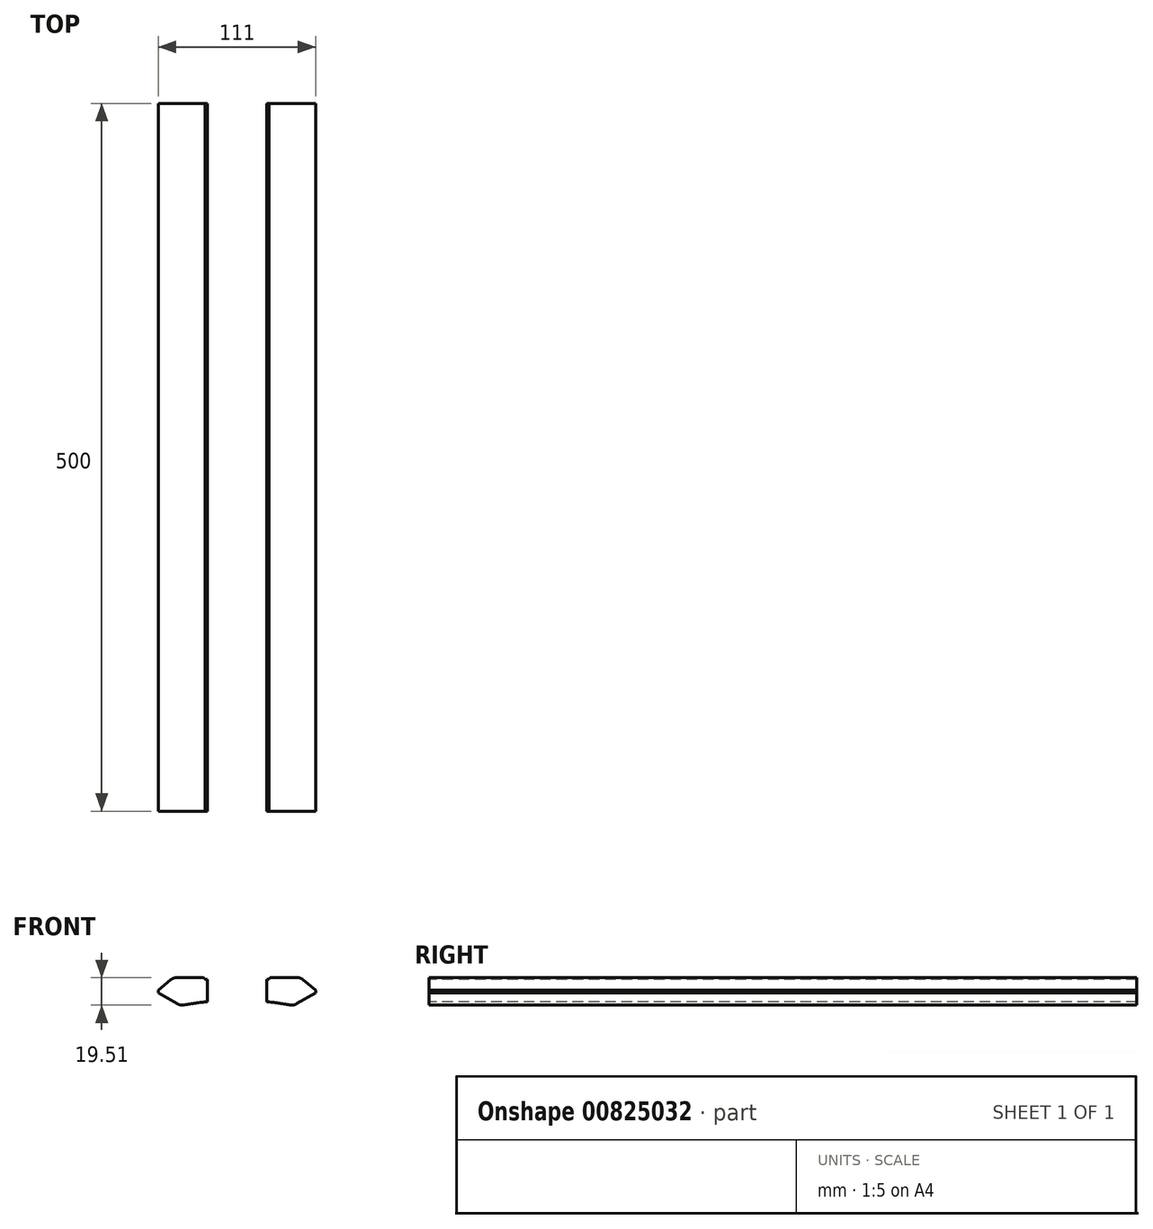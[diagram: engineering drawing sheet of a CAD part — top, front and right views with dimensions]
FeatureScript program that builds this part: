
annotation { "Feature Type Name" : "Feature", "Feature Type Description" : "" }
export const myFeature = defineFeature(function(context is Context, id is Id, definition is map)
    precondition{}
    {
        {
            var Q0;
            Q0=qCreatedBy(makeId("Front.planeOp"),FACE);
            var sketch = newSketch(context, id + "F0", { "sketchPlane" : qUnion([Q0])});
            skLineSegment(sketch, "E0", {"start": v(0, 30) * mm, "end": v(0, -27.09) * mm, "construction": true});
            skLineSegment(sketch, "E1", {"start": v(-40.18, -7.33) * mm, "end": v(-57.5, 2.67) * mm});
            skLineSegment(sketch, "E2", {"start": v(-57.5, 2.67) * mm, "end": v(-57.5, 6.67) * mm});
            skLineSegment(sketch, "E3", {"start": v(-57.5, 6.67) * mm, "end": v(-45.58, 16.67) * mm});
            skLineSegment(sketch, "E4", {"start": v(-45.58, 16.67) * mm, "end": v(-22.5, 16.67) * mm});
            skLineSegment(sketch, "E5", {"start": v(-22.5, 16.67) * mm, "end": v(-22.5, 15.37) * mm});
            skLineSegment(sketch, "E6", {"start": v(-22.5, 15.37) * mm, "end": v(0, 15.37) * mm});
            skLineSegment(sketch, "E7.MirrorCS", {"start": v(40.18, -7.33) * mm, "end": v(57.5, 2.67) * mm});
            skLineSegment(sketch, "E8.MirrorCS", {"start": v(57.5, 2.67) * mm, "end": v(57.5, 6.67) * mm});
            skLineSegment(sketch, "E9.MirrorCS", {"start": v(57.5, 6.67) * mm, "end": v(45.58, 16.67) * mm});
            skLineSegment(sketch, "E10.MirrorCS", {"start": v(22.5, 15.37) * mm, "end": v(0, 15.37) * mm});
            skLineSegment(sketch, "E11.MirrorCS", {"start": v(22.5, 16.67) * mm, "end": v(22.5, 15.37) * mm});
            skLineSegment(sketch, "E12.MirrorCS", {"start": v(45.58, 16.67) * mm, "end": v(22.5, 16.67) * mm});
            skArc(sketch, "E13", {"start": v(40.18, -7.33) * mm, "mid": v(0, -3.25) * mm, "end": v(-40.18, -7.33) * mm});
            skSolve(sketch);
        }
        {
            var Q0;
            Q0=makeQuery(id+"F0.imprint","IMPRINT",FACE,{"disambiguationData":[TD([[makeQuery(id+"F0.imprint","IMPRINT",EDGE,{"derivedFrom":sQuery(id+"F0.wireOp",EDGE,"E1")}),-1.0]])]});
            extrude(context, id + "F1", {"entities" : qUnion([Q0]), "endBound" : BoundingType.SYMMETRIC, "depth" : 500 * mm, "offsetDistance" : 25 * mm});
        }
        {
            var Q0;
            Q0=makeQuery(id+"F1.opExtrude","CAP_FACE",FACE,{"disambiguationData":[OSD([sQuery(id+"F0.wireOp",EDGE,"E1"),sQuery(id+"F0.wireOp",EDGE,"E2"),sQuery(id+"F0.wireOp",EDGE,"E3"),sQuery(id+"F0.wireOp",EDGE,"E4"),sQuery(id+"F0.wireOp",EDGE,"E5"),sQuery(id+"F0.wireOp",EDGE,"E6"),sQuery(id+"F0.wireOp",EDGE,"E7.MirrorCS"),sQuery(id+"F0.wireOp",EDGE,"E8.MirrorCS"),sQuery(id+"F0.wireOp",EDGE,"E9.MirrorCS"),sQuery(id+"F0.wireOp",EDGE,"E10.MirrorCS"),sQuery(id+"F0.wireOp",EDGE,"E11.MirrorCS"),sQuery(id+"F0.wireOp",EDGE,"E12.MirrorCS"),sQuery(id+"F0.wireOp",EDGE,"E13")])],"isStart":false});
            var sketch = newSketch(context, id + "F2", { "sketchPlane" : qUnion([Q0])});
            skLineSegment(sketch, "E14.bottom", {"start": v(19, 0) * mm, "end": v(-19, 0) * mm});
            skLineSegment(sketch, "E14.top", {"start": v(19, 13.37) * mm, "end": v(-19, 13.37) * mm});
            skLineSegment(sketch, "E14.left", {"start": v(19, 0) * mm, "end": v(19, 13.37) * mm});
            skLineSegment(sketch, "E14.right", {"start": v(-19, 0) * mm, "end": v(-19, 13.37) * mm});
            skPoint(sketch, "E14.middle", {"position": v(0, 6.69) * mm});
            skSolve(sketch);
        }
        {
            var Q0;
            Q0=makeQuery(id+"F2.imprint","IMPRINT",FACE,{"disambiguationData":[TD([[makeQuery(id+"F2.imprint","IMPRINT",EDGE,{"derivedFrom":sQuery(id+"F2.wireOp",EDGE,"E14.bottom")}),-1.0]])]});
            extrude(context, id + "F3", {"entities" : qUnion([Q0]), "operationType" : NewBodyOperationType.REMOVE, "oppositeDirection" : true, "depth" : 1200 * mm, "offsetDistance" : 25 * mm});
        }
        {
            var Q0;
            Q0=makeQuery(id+"F1.opExtrude","SWEPT_EDGE",EDGE,{"disambiguationData":[OSD([sQuery(id+"F0.wireOp",EDGE,"E4"),sQuery(id+"F0.wireOp",EDGE,"E5")])]});
            var Q1;
            Q1=makeQuery(id+"F1.opExtrude","SWEPT_EDGE",EDGE,{"disambiguationData":[OSD([sQuery(id+"F0.wireOp",EDGE,"E11.MirrorCS"),sQuery(id+"F0.wireOp",EDGE,"E12.MirrorCS")])]});
            fillet(context, id + "F4", {"entities" : qUnion([Q0, Q1]), "radius" : 2 * mm, "tangentPropagation" : true, "allowEdgeOverflow" : false});
        }
        {
            var Q0;
            Q0=makeQuery(id+"F1.opExtrude","SWEPT_EDGE",EDGE,{"disambiguationData":[OSD([sQuery(id+"F0.wireOp",EDGE,"E9.MirrorCS"),sQuery(id+"F0.wireOp",EDGE,"E12.MirrorCS")])]});
            var Q1;
            Q1=makeQuery(id+"F1.opExtrude","SWEPT_EDGE",EDGE,{"disambiguationData":[OSD([sQuery(id+"F0.wireOp",EDGE,"E7.MirrorCS"),sQuery(id+"F0.wireOp",EDGE,"E13")])]});
            var Q2;
            Q2=makeQuery(id+"F1.opExtrude","SWEPT_EDGE",EDGE,{"disambiguationData":[OSD([sQuery(id+"F0.wireOp",EDGE,"E3"),sQuery(id+"F0.wireOp",EDGE,"E4")])]});
            var Q3;
            Q3=makeQuery(id+"F1.opExtrude","SWEPT_EDGE",EDGE,{"disambiguationData":[OSD([sQuery(id+"F0.wireOp",EDGE,"E1"),sQuery(id+"F0.wireOp",EDGE,"E13")])]});
            fillet(context, id + "F5", {"entities" : qUnion([Q0, Q1, Q2, Q3]), "radius" : 9 * mm, "tangentPropagation" : true, "allowEdgeOverflow" : false});
        }
        {
            var Q0;
            Q0=makeQuery(id+"F1.opExtrude","SWEPT_EDGE",EDGE,{"disambiguationData":[OSD([sQuery(id+"F0.wireOp",EDGE,"E2"),sQuery(id+"F0.wireOp",EDGE,"E3")])]});
            var Q1;
            Q1=makeQuery(id+"F1.opExtrude","SWEPT_EDGE",EDGE,{"disambiguationData":[OSD([sQuery(id+"F0.wireOp",EDGE,"E1"),sQuery(id+"F0.wireOp",EDGE,"E2")])]});
            var Q2;
            Q2=makeQuery(id+"F1.opExtrude","SWEPT_EDGE",EDGE,{"disambiguationData":[OSD([sQuery(id+"F0.wireOp",EDGE,"E8.MirrorCS"),sQuery(id+"F0.wireOp",EDGE,"E9.MirrorCS")])]});
            var Q3;
            Q3=makeQuery(id+"F1.opExtrude","SWEPT_EDGE",EDGE,{"disambiguationData":[OSD([sQuery(id+"F0.wireOp",EDGE,"E7.MirrorCS"),sQuery(id+"F0.wireOp",EDGE,"E8.MirrorCS")])]});
            fillet(context, id + "F6", {"entities" : qUnion([Q0, Q1, Q2, Q3]), "radius" : 1 * mm, "tangentPropagation" : true, "allowEdgeOverflow" : false});
        }
        {
            var Q0;
            Q0=makeQuery(id+"F1.opExtrude","CAP_FACE",FACE,{"disambiguationData":[OSD([sQuery(id+"F0.wireOp",EDGE,"E1"),sQuery(id+"F0.wireOp",EDGE,"E2"),sQuery(id+"F0.wireOp",EDGE,"E3"),sQuery(id+"F0.wireOp",EDGE,"E4"),sQuery(id+"F0.wireOp",EDGE,"E5"),sQuery(id+"F0.wireOp",EDGE,"E6"),sQuery(id+"F0.wireOp",EDGE,"E7.MirrorCS"),sQuery(id+"F0.wireOp",EDGE,"E8.MirrorCS"),sQuery(id+"F0.wireOp",EDGE,"E9.MirrorCS"),sQuery(id+"F0.wireOp",EDGE,"E10.MirrorCS"),sQuery(id+"F0.wireOp",EDGE,"E11.MirrorCS"),sQuery(id+"F0.wireOp",EDGE,"E12.MirrorCS"),sQuery(id+"F0.wireOp",EDGE,"E13")])],"isStart":false});
            var sketch = newSketch(context, id + "F7", { "sketchPlane" : qUnion([Q0])});
            skLineSegment(sketch, "E15.0.0", {"start": v(-48.1, 14.57) * mm, "end": v(-57.14, 6.97) * mm});
            skArc(sketch, "E15.0.1", {"start": v(-57.14, 6.97) * mm, "mid": v(-57.4, 6.63) * mm, "end": v(-57.5, 6.2) * mm});
            skLineSegment(sketch, "E15.0.2", {"start": v(-57.5, 6.2) * mm, "end": v(-57.5, 3.25) * mm});
            skArc(sketch, "E15.0.3", {"start": v(-57.5, 3.25) * mm, "mid": v(-57.37, 2.75) * mm, "end": v(-57, 2.39) * mm});
            skLineSegment(sketch, "E15.0.4", {"start": v(-57, 2.39) * mm, "end": v(-43.1, -5.64) * mm});
            skArc(sketch, "E15.0.5", {"start": v(-43.1, -5.64) * mm, "mid": v(-40.12, -6.72) * mm, "end": v(-36.94, -6.69) * mm});
            skArc(sketch, "E15.0.6", {"start": v(-36.94, -6.69) * mm, "mid": v(0, -3.25) * mm, "end": v(36.94, -6.69) * mm});
            skArc(sketch, "E15.0.7", {"start": v(36.94, -6.69) * mm, "mid": v(40.12, -6.72) * mm, "end": v(43.1, -5.64) * mm});
            skLineSegment(sketch, "E15.0.8", {"start": v(43.1, -5.64) * mm, "end": v(57, 2.39) * mm});
            skArc(sketch, "E15.0.9", {"start": v(57, 2.39) * mm, "mid": v(57.37, 2.75) * mm, "end": v(57.5, 3.25) * mm});
            skLineSegment(sketch, "E15.0.10", {"start": v(57.5, 3.25) * mm, "end": v(57.5, 6.2) * mm});
            skArc(sketch, "E15.0.11", {"start": v(57.5, 6.2) * mm, "mid": v(57.4, 6.63) * mm, "end": v(57.14, 6.97) * mm});
            skLineSegment(sketch, "E15.0.12", {"start": v(57.14, 6.97) * mm, "end": v(48.1, 14.57) * mm});
            skArc(sketch, "E15.0.13", {"start": v(48.1, 14.57) * mm, "mid": v(45.38, 16.13) * mm, "end": v(42.3, 16.67) * mm});
            skLineSegment(sketch, "E15.0.14", {"start": v(42.3, 16.67) * mm, "end": v(24.37, 16.67) * mm});
            skArc(sketch, "E15.0.15", {"start": v(24.37, 16.67) * mm, "mid": v(23.23, 16.32) * mm, "end": v(22.5, 15.37) * mm});
            skLineSegment(sketch, "E15.0.16", {"start": v(22.5, 15.37) * mm, "end": v(-22.5, 15.37) * mm});
            skArc(sketch, "E15.0.17", {"start": v(-22.5, 15.37) * mm, "mid": v(-23.23, 16.32) * mm, "end": v(-24.37, 16.67) * mm});
            skLineSegment(sketch, "E15.0.18", {"start": v(-24.37, 16.67) * mm, "end": v(-42.3, 16.67) * mm});
            skArc(sketch, "E15.0.19", {"start": v(-42.3, 16.67) * mm, "mid": v(-45.38, 16.13) * mm, "end": v(-48.1, 14.57) * mm});
            skArc(sketch, "E16.0", {"start": v(-37.3, -4.72) * mm, "mid": v(-29.18, -3.37) * mm, "end": v(-21, -2.34) * mm});
            skArc(sketch, "E16.1", {"start": v(-42.1, -3.9) * mm, "mid": v(-39.78, -4.74) * mm, "end": v(-37.3, -4.72) * mm});
            skLineSegment(sketch, "E16.2", {"start": v(-55.5, 3.83) * mm, "end": v(-42.1, -3.9) * mm});
            skLineSegment(sketch, "E16.3", {"start": v(-24.37, 14.67) * mm, "end": v(-42.3, 14.67) * mm});
            skArc(sketch, "E16.4", {"start": v(-42.3, 14.67) * mm, "mid": v(-44.7, 14.25) * mm, "end": v(-46.8, 13.04) * mm});
            skLineSegment(sketch, "E16.5", {"start": v(-46.8, 13.04) * mm, "end": v(-55.5, 5.74) * mm});
            skLineSegment(sketch, "E16.6", {"start": v(-55.5, 5.74) * mm, "end": v(-55.5, 3.83) * mm});
            skLineSegment(sketch, "E17.0", {"start": v(-21, -2.34) * mm, "end": v(-21, 13.37) * mm});
            skLineSegment(sketch, "E18.0", {"start": v(-21, 13.37) * mm, "end": v(-22.5, 13.37) * mm});
            skArc(sketch, "E19", {"start": v(-22.5, 13.37) * mm, "mid": v(-23.23, 14.32) * mm, "end": v(-24.37, 14.67) * mm});
            skArc(sketch, "E20.MirrorCS", {"start": v(22.5, 13.37) * mm, "mid": v(23.23, 14.32) * mm, "end": v(24.37, 14.67) * mm});
            skLineSegment(sketch, "E21.MirrorCS", {"start": v(21, 13.37) * mm, "end": v(22.5, 13.37) * mm});
            skLineSegment(sketch, "E22.MirrorCS", {"start": v(21, -2.34) * mm, "end": v(21, 13.37) * mm});
            skArc(sketch, "E23.MirrorCS", {"start": v(37.3, -4.72) * mm, "mid": v(29.18, -3.37) * mm, "end": v(21, -2.34) * mm});
            skArc(sketch, "E24.MirrorCS", {"start": v(42.1, -3.9) * mm, "mid": v(39.78, -4.74) * mm, "end": v(37.3, -4.72) * mm});
            skLineSegment(sketch, "E25.MirrorCS", {"start": v(55.5, 3.83) * mm, "end": v(42.1, -3.9) * mm});
            skLineSegment(sketch, "E26.MirrorCS", {"start": v(55.5, 5.74) * mm, "end": v(55.5, 3.83) * mm});
            skLineSegment(sketch, "E27.MirrorCS", {"start": v(46.8, 13.04) * mm, "end": v(55.5, 5.74) * mm});
            skArc(sketch, "E28.MirrorCS", {"start": v(42.3, 14.67) * mm, "mid": v(44.7, 14.25) * mm, "end": v(46.8, 13.04) * mm});
            skLineSegment(sketch, "E29.MirrorCS", {"start": v(24.37, 14.67) * mm, "end": v(42.3, 14.67) * mm});
            skSolve(sketch);
        }
        {
            var Q0;
            Q0=makeQuery(id+"F7.imprint","IMPRINT",FACE,{"disambiguationData":[TD([[makeQuery(id+"F7.imprint","IMPRINT",EDGE,{"derivedFrom":sQuery(id+"F7.wireOp",EDGE,"E16.0")}),1.0]])]});
            var Q1;
            Q1=makeQuery(id+"F7.imprint","IMPRINT",FACE,{"disambiguationData":[TD([[makeQuery(id+"F7.imprint","IMPRINT",EDGE,{"derivedFrom":sQuery(id+"F7.wireOp",EDGE,"E20.MirrorCS")}),-1.0]])]});
            extrude(context, id + "F8", {"entities" : qUnion([Q0, Q1]), "operationType" : NewBodyOperationType.REMOVE, "endBound" : BoundingType.THROUGH_ALL, "oppositeDirection" : true, "depth" : 25 * mm, "offsetDistance" : 25 * mm});
        }
    });
